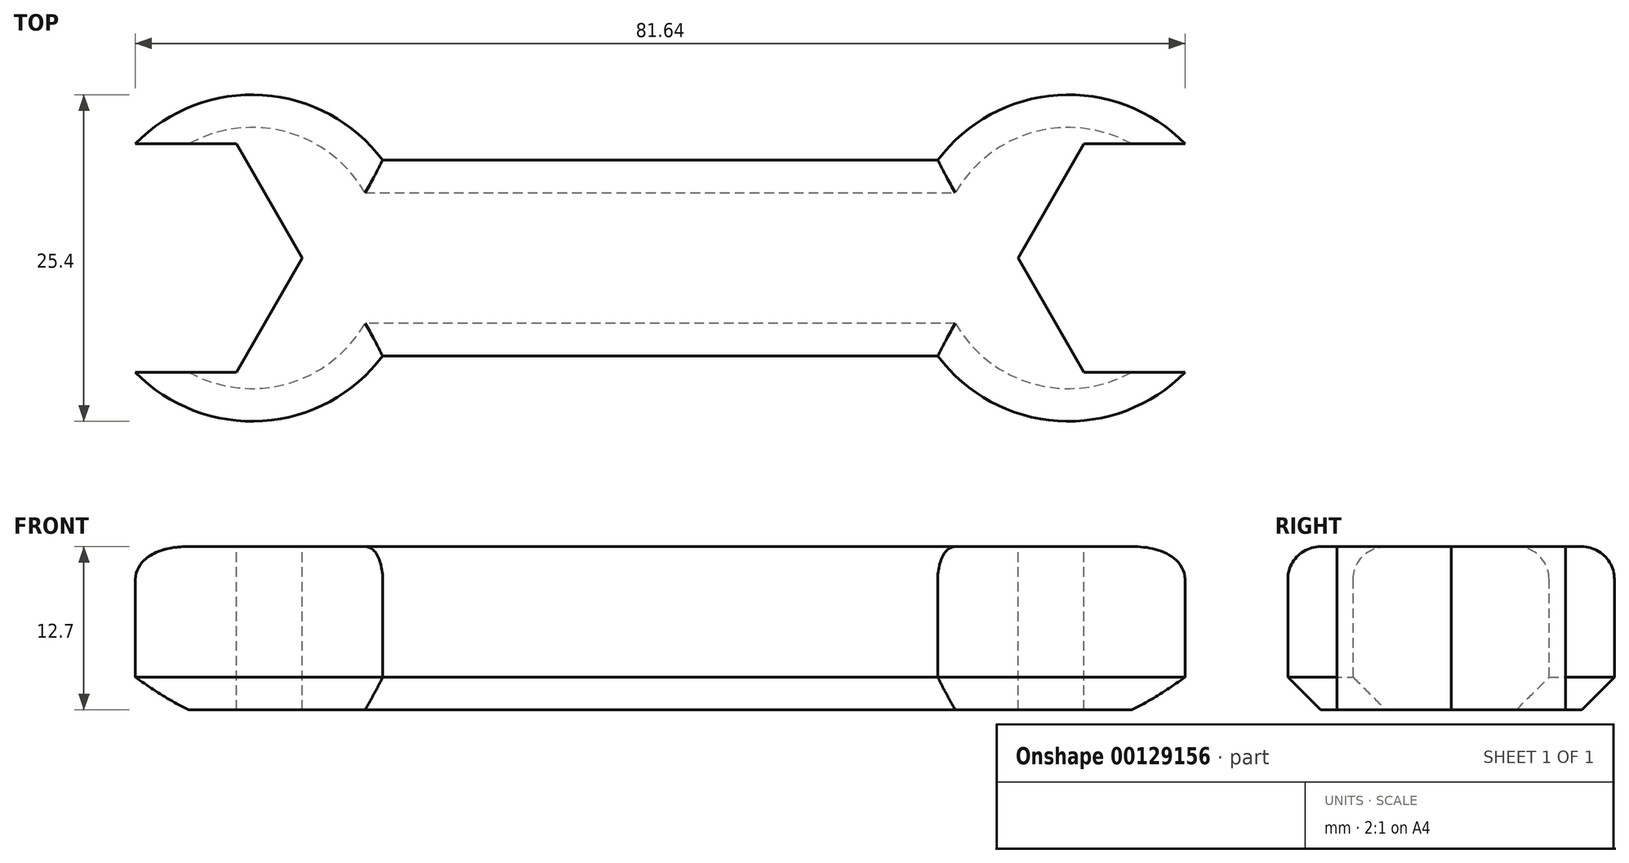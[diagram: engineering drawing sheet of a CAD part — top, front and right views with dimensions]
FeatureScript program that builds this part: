
annotation { "Feature Type Name" : "Feature", "Feature Type Description" : "" }
export const myFeature = defineFeature(function(context is Context, id is Id, definition is map)
    precondition{}
    {
        {
            var Q0;
            Q0=qCreatedBy(makeId("Top.planeOp"),FACE);
            var sketch = newSketch(context, id + "F0", { "sketchPlane" : qUnion([Q0])});
            skArc(sketch, "E0", {"start": v(-21.59, 7.62) * mm, "mid": v(-44.45, 0) * mm, "end": v(-21.59, -7.62) * mm});
            skArc(sketch, "E1", {"start": v(21.59, -7.62) * mm, "mid": v(44.45, 0) * mm, "end": v(21.59, 7.62) * mm});
            skLineSegment(sketch, "E2", {"start": v(-21.59, 7.62) * mm, "end": v(21.59, 7.62) * mm});
            skLineSegment(sketch, "E3", {"start": v(-21.59, -7.62) * mm, "end": v(21.59, -7.62) * mm});
            skLineSegment(sketch, "E4", {"start": v(-31.75, 0) * mm, "end": v(31.75, 0) * mm, "construction": true});
            skSolve(sketch);
        }
        {
            var Q0;
            Q0 = qSketchRegion(id + "F0", true);
            extrude(context, id + "F1", {"entities" : qUnion([Q0]), "endBound" : BoundingType.SYMMETRIC, "oppositeDirection" : true, "depth" : 12.7 * mm});
        }
        {
            var Q0;
            Q0=makeQuery(id+"F1.opExtrude","CAP_FACE",FACE,{"disambiguationData":[OSD([sQuery(id+"F0.wireOp",EDGE,"E0"),sQuery(id+"F0.wireOp",EDGE,"E1"),sQuery(id+"F0.wireOp",EDGE,"E2"),sQuery(id+"F0.wireOp",EDGE,"E3")])],"isStart":true});
            var sketch = newSketch(context, id + "F2", { "sketchPlane" : qUnion([Q0])});
            skCircle(sketch, "E5.cCircle", {"center": v(-38.1, 0) * mm, "radius": 8.9 * mm, "construction": true});
            skLineSegment(sketch, "E5.0", {"start": v(-48.37, 0) * mm, "end": v(-43.23, 8.89) * mm});
            skLineSegment(sketch, "E5.1", {"start": v(-43.23, 8.89) * mm, "end": v(-32.97, 8.89) * mm});
            skLineSegment(sketch, "E5.2", {"start": v(-32.97, 8.89) * mm, "end": v(-27.83, 0) * mm});
            skLineSegment(sketch, "E5.3", {"start": v(-27.83, 0) * mm, "end": v(-32.97, -8.9) * mm});
            skLineSegment(sketch, "E5.4", {"start": v(-32.97, -8.9) * mm, "end": v(-43.23, -8.9) * mm});
            skLineSegment(sketch, "E5.5", {"start": v(-43.23, -8.9) * mm, "end": v(-48.37, 0) * mm});
            skPoint(sketch, "E5.0.midPoint", {"position": v(-45.8, 4.45) * mm});
            skSolve(sketch);
        }
        {
            var Q0;
            Q0 = qSketchRegion(id + "F2", true);
            extrude(context, id + "F3", {"entities" : qUnion([Q0]), "endBound" : BoundingType.THROUGH_ALL, "oppositeDirection" : true, "depth" : 25.4 * mm});
        }
        {
            var Q0;
            Q0=makeQuery(id+"F3.opExtrude","SWEPT_BODY",BODY,{"disambiguationData":[OSD([sQuery(id+"F2.wireOp",EDGE,"E5.0"),sQuery(id+"F2.wireOp",EDGE,"E5.1"),sQuery(id+"F2.wireOp",EDGE,"E5.2"),sQuery(id+"F2.wireOp",EDGE,"E5.3"),sQuery(id+"F2.wireOp",EDGE,"E5.4"),sQuery(id+"F2.wireOp",EDGE,"E5.5")])]});
            var Q1;
            Q1=qCreatedBy(makeId("Right.planeOp"),FACE);
            mirror(context, id + "F4", {"operationType" : NewBodyOperationType.REMOVE, "entities" : qUnion([Q0]), "mirrorPlane" : qUnion([Q1])});
        }
        {
            var Q0;
            Q0=makeQuery(id+"F3.opExtrude","SWEPT_BODY",BODY,{"disambiguationData":[OSD([sQuery(id+"F2.wireOp",EDGE,"E5.0"),sQuery(id+"F2.wireOp",EDGE,"E5.1"),sQuery(id+"F2.wireOp",EDGE,"E5.2"),sQuery(id+"F2.wireOp",EDGE,"E5.3"),sQuery(id+"F2.wireOp",EDGE,"E5.4"),sQuery(id+"F2.wireOp",EDGE,"E5.5")])]});
            var Q1;
            Q1=makeQuery(id+"F1.opExtrude","SWEPT_BODY",BODY,{"disambiguationData":[OSD([sQuery(id+"F0.wireOp",EDGE,"E0"),sQuery(id+"F0.wireOp",EDGE,"E1"),sQuery(id+"F0.wireOp",EDGE,"E2"),sQuery(id+"F0.wireOp",EDGE,"E3")])]});
            booleanBodies(context, id + "F5", {"operationType" : BooleanOperationType.SUBTRACTION, "tools" : qUnion([Q0]), "targets" : qUnion([Q1])});
        }
        {
            var Q0;
            {var subQ0=sQuery(id+"F0.wireOp",EDGE,"E0");var subQ1=sQuery(id+"F0.wireOp",EDGE,"E3");Q0=makeQuery(id+"F5.opBoolean","SPLIT",EDGE,{"disambiguationData":[TD([makeQuery(id+"F1.opExtrude","SWEPT_FACE",FACE,{"disambiguationData":[OSD([subQ1])]})])],"derivedFrom":makeQuery(id+"F1.opExtrude","CAP_EDGE",EDGE,{"disambiguationData":[OSD([subQ0])],"isStart":true})});}
            var Q1;
            Q1=makeQuery(id+"F1.opExtrude","CAP_EDGE",EDGE,{"disambiguationData":[OSD([sQuery(id+"F0.wireOp",EDGE,"E3")])],"isStart":true});
            var Q2;
            {var subQ0=sQuery(id+"F0.wireOp",EDGE,"E3");var subQ1=sQuery(id+"F0.wireOp",EDGE,"E1");Q2=makeQuery(id+"F4.boolean.opBoolean","SPLIT",EDGE,{"disambiguationData":[TD([makeQuery(id+"F1.opExtrude","SWEPT_FACE",FACE,{"disambiguationData":[OSD([subQ0])]})])],"derivedFrom":makeQuery(id+"F1.opExtrude","CAP_EDGE",EDGE,{"disambiguationData":[OSD([subQ1])],"isStart":true})});}
            var Q3;
            {var subQ0=sQuery(id+"F0.wireOp",EDGE,"E2");var subQ1=sQuery(id+"F0.wireOp",EDGE,"E1");Q3=makeQuery(id+"F4.boolean.opBoolean","SPLIT",EDGE,{"disambiguationData":[TD([makeQuery(id+"F1.opExtrude","SWEPT_FACE",FACE,{"disambiguationData":[OSD([subQ0])]})])],"derivedFrom":makeQuery(id+"F1.opExtrude","CAP_EDGE",EDGE,{"disambiguationData":[OSD([subQ1])],"isStart":true})});}
            var Q4;
            Q4=makeQuery(id+"F1.opExtrude","CAP_EDGE",EDGE,{"disambiguationData":[OSD([sQuery(id+"F0.wireOp",EDGE,"E2")])],"isStart":true});
            var Q5;
            {var subQ0=sQuery(id+"F0.wireOp",EDGE,"E0");var subQ1=sQuery(id+"F0.wireOp",EDGE,"E2");Q5=makeQuery(id+"F5.opBoolean","SPLIT",EDGE,{"disambiguationData":[TD([makeQuery(id+"F1.opExtrude","SWEPT_FACE",FACE,{"disambiguationData":[OSD([subQ1])]})])],"derivedFrom":makeQuery(id+"F1.opExtrude","CAP_EDGE",EDGE,{"disambiguationData":[OSD([subQ0])],"isStart":true})});}
            fillet(context, id + "F6", {"entities" : qUnion([Q0, Q1, Q2, Q3, Q4, Q5]), "radius" : 2.54 * mm, "tangentPropagation" : true, "allowEdgeOverflow" : false});
        }
        {
            var Q0;
            {var subQ0=sQuery(id+"F0.wireOp",EDGE,"E0");var subQ1=sQuery(id+"F0.wireOp",EDGE,"E2");Q0=makeQuery(id+"F5.opBoolean","SPLIT",EDGE,{"disambiguationData":[TD([makeQuery(id+"F1.opExtrude","SWEPT_FACE",FACE,{"disambiguationData":[OSD([subQ1])]})])],"derivedFrom":makeQuery(id+"F1.opExtrude","CAP_EDGE",EDGE,{"disambiguationData":[OSD([subQ0])],"isStart":false})});}
            var Q1;
            Q1=makeQuery(id+"F1.opExtrude","CAP_EDGE",EDGE,{"disambiguationData":[OSD([sQuery(id+"F0.wireOp",EDGE,"E2")])],"isStart":false});
            var Q2;
            {var subQ0=sQuery(id+"F0.wireOp",EDGE,"E2");var subQ1=sQuery(id+"F0.wireOp",EDGE,"E1");Q2=makeQuery(id+"F4.boolean.opBoolean","SPLIT",EDGE,{"disambiguationData":[TD([makeQuery(id+"F1.opExtrude","SWEPT_FACE",FACE,{"disambiguationData":[OSD([subQ0])]})])],"derivedFrom":makeQuery(id+"F1.opExtrude","CAP_EDGE",EDGE,{"disambiguationData":[OSD([subQ1])],"isStart":false})});}
            var Q3;
            {var subQ0=sQuery(id+"F0.wireOp",EDGE,"E3");var subQ1=sQuery(id+"F0.wireOp",EDGE,"E1");Q3=makeQuery(id+"F4.boolean.opBoolean","SPLIT",EDGE,{"disambiguationData":[TD([makeQuery(id+"F1.opExtrude","SWEPT_FACE",FACE,{"disambiguationData":[OSD([subQ0])]})])],"derivedFrom":makeQuery(id+"F1.opExtrude","CAP_EDGE",EDGE,{"disambiguationData":[OSD([subQ1])],"isStart":false})});}
            var Q4;
            Q4=makeQuery(id+"F1.opExtrude","CAP_EDGE",EDGE,{"disambiguationData":[OSD([sQuery(id+"F0.wireOp",EDGE,"E3")])],"isStart":false});
            var Q5;
            {var subQ0=sQuery(id+"F0.wireOp",EDGE,"E0");var subQ1=sQuery(id+"F0.wireOp",EDGE,"E3");Q5=makeQuery(id+"F5.opBoolean","SPLIT",EDGE,{"disambiguationData":[TD([makeQuery(id+"F1.opExtrude","SWEPT_FACE",FACE,{"disambiguationData":[OSD([subQ1])]})])],"derivedFrom":makeQuery(id+"F1.opExtrude","CAP_EDGE",EDGE,{"disambiguationData":[OSD([subQ0])],"isStart":false})});}
            chamfer(context, id + "F7", {"entities" : qUnion([Q0, Q1, Q2, Q3, Q4, Q5]), "width" : 2.54 * mm, "tangentPropagation" : true});
        }
    });
